# Revit family: WH2898-ADA-EG10-1.28
name_source: partatom
category: Plumbing Fixtures
revit_build: Autodesk Revit MEP 2016 (Build: 20150220_1215(x64)
units: mm (PartAtom-declared; Revit-internal decimal feet)

## family parameters
Cut with Voids When Loaded = No
Host = Face
OmniClass Number = 23.45.05.21
OmniClass Title = Plumbing Fixtures - Sanitary Disposal Units
Part Type = Normal
Room Calculation Point = No
Round Connector Dimension = Use Diameter
Shared = Yes

## types (1)
- WH2898-ADA-EG-1.28
    Amperage = 0
    CW Connection = Yes
    Default Elevation = 36"
    Description = Ligature Resistant Flush Valve Cover With 1.28 GPF Hydraulic Flush Valve (White)
    HW Connection = Yes
    Manufacturer = Whitehall
    Material = Type 304 Stainless Steel
    Model = WH2898-ADA-EG10-1.28
    Revised Date = 10/01/19
    Tempered Water Connection = No
    URL = https://www.whitehallmfg.com
    Vent Connection = No
    Voltage = 0
    WH2898-ADA-EG10-1.28 - Ligature Resistant Flush Valve Cover With 1.28 GPF Hydraulic Flush Valve (White) = Yes
    Waste Connection = No

## geometry (parser evidence)
native form markers: Sweep x9
no freeform markers — native parametric forms only
